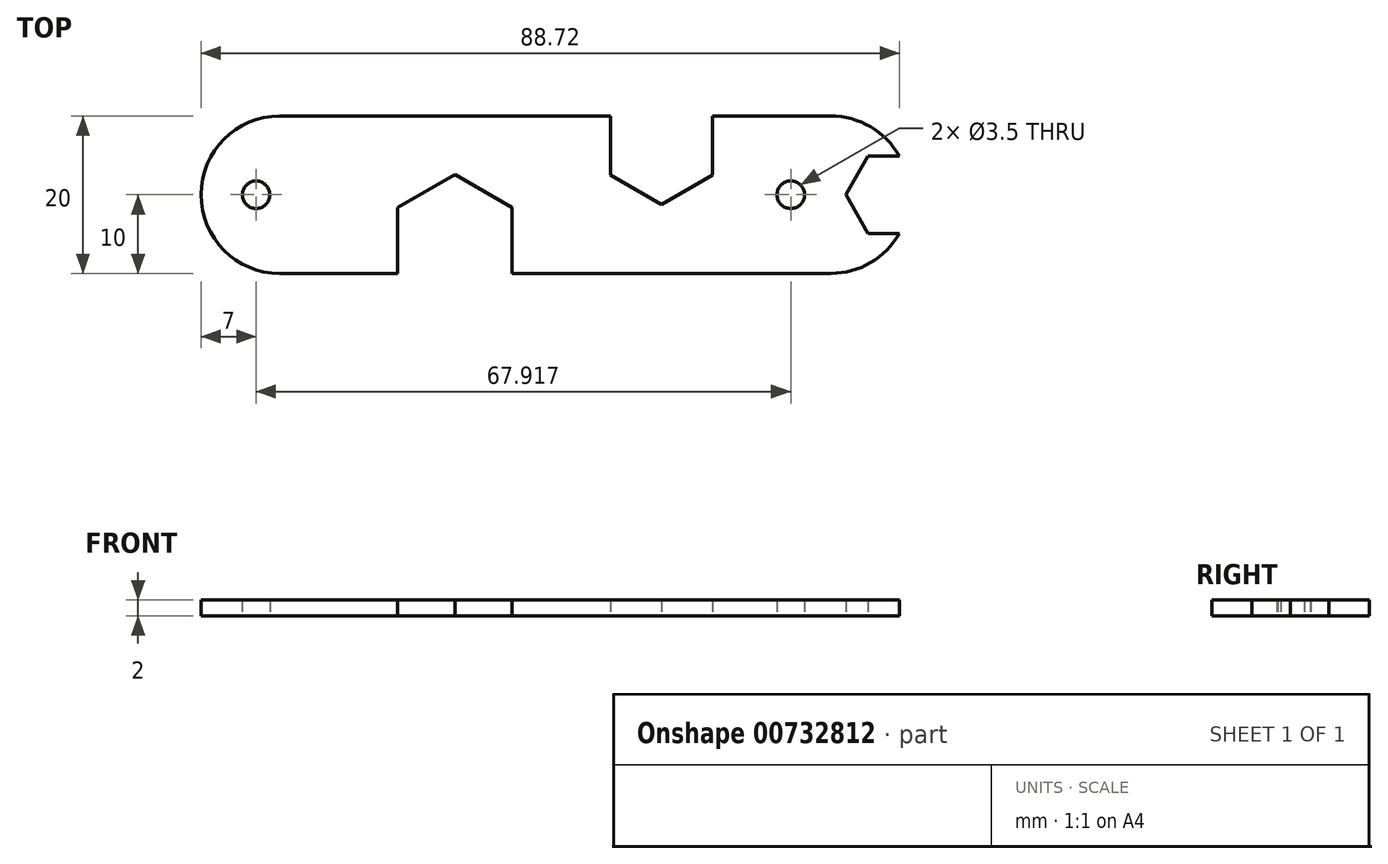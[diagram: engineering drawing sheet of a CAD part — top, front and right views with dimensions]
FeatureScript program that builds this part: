
annotation { "Feature Type Name" : "Feature", "Feature Type Description" : "" }
export const myFeature = defineFeature(function(context is Context, id is Id, definition is map)
    precondition{}
    {
        {
            var Q0;
            Q0=qCreatedBy(makeId("Top.planeOp"),FACE);
            var sketch = newSketch(context, id + "F0", { "sketchPlane" : qUnion([Q0])});
            skArc(sketch, "E0", {"start": v(36.44, 10) * mm, "mid": v(26.44, 0) * mm, "end": v(36.44, -10) * mm});
            skArc(sketch, "E1", {"start": v(106.44, -10) * mm, "mid": v(111.57, -8.59) * mm, "end": v(115.24, -4.74) * mm});
            skLineSegment(sketch, "E2", {"start": v(36.44, -10) * mm, "end": v(51.44, -10) * mm});
            skLineSegment(sketch, "E3", {"start": v(106.44, 10) * mm, "end": v(91.44, 10) * mm});
            skCircle(sketch, "E4.cCircle", {"center": v(58.69, -5.81) * mm, "radius": 7.25 * mm, "construction": true});
            skLineSegment(sketch, "E4.0", {"start": v(51.44, -10) * mm, "end": v(51.44, -1.63) * mm});
            skLineSegment(sketch, "E4.1", {"start": v(51.44, -1.63) * mm, "end": v(58.69, 2.56) * mm});
            skLineSegment(sketch, "E4.2", {"start": v(58.69, 2.56) * mm, "end": v(65.94, -1.63) * mm});
            skLineSegment(sketch, "E4.3", {"start": v(65.94, -1.63) * mm, "end": v(65.94, -10) * mm});
            skPoint(sketch, "E4.0.midPoint", {"position": v(51.44, -5.81) * mm});
            skCircle(sketch, "E5.cCircle", {"center": v(84.94, 6.25) * mm, "radius": 6.5 * mm, "construction": true});
            skLineSegment(sketch, "E5.0", {"start": v(78.44, 2.5) * mm, "end": v(78.44, 10) * mm});
            skLineSegment(sketch, "E5.3", {"start": v(91.44, 10) * mm, "end": v(91.44, 2.5) * mm});
            skLineSegment(sketch, "E5.4", {"start": v(91.44, 2.5) * mm, "end": v(84.94, -1.26) * mm});
            skLineSegment(sketch, "E5.5", {"start": v(84.94, -1.26) * mm, "end": v(78.44, 2.5) * mm});
            skPoint(sketch, "E5.0.midPoint", {"position": v(78.44, 6.25) * mm});
            skCircle(sketch, "E6.cCircle", {"center": v(114.01, 0) * mm, "radius": 4.9 * mm, "construction": true});
            skLineSegment(sketch, "E6.0", {"start": v(115.16, -4.9) * mm, "end": v(111.19, -4.9) * mm});
            skLineSegment(sketch, "E6.1", {"start": v(111.19, -4.9) * mm, "end": v(108.36, 0) * mm});
            skLineSegment(sketch, "E6.2", {"start": v(108.36, 0) * mm, "end": v(111.19, 4.9) * mm});
            skLineSegment(sketch, "E6.3", {"start": v(111.19, 4.9) * mm, "end": v(115.16, 4.9) * mm});
            skPoint(sketch, "E6.0.midPoint", {"position": v(114.01, -4.9) * mm});
            skCircle(sketch, "E7", {"center": v(33.44, 0) * mm, "radius": 1.75 * mm});
            skCircle(sketch, "E8", {"center": v(101.36, 0) * mm, "radius": 1.75 * mm});
            skArc(sketch, "E9.trimOffspring", {"start": v(115.24, 4.74) * mm, "mid": v(111.57, 8.59) * mm, "end": v(106.44, 10) * mm});
            skPoint(sketch, "E10.orphan", {"position": v(116.84, 4.9) * mm});
            skPoint(sketch, "E6.5.end.orphan", {"position": v(116.84, -4.9) * mm});
            skLineSegment(sketch, "E11.trimOffspring", {"start": v(78.44, 10) * mm, "end": v(36.44, 10) * mm});
            skPoint(sketch, "E12.orphan", {"position": v(84.94, 13.75) * mm});
            skLineSegment(sketch, "E13.trimOffspring", {"start": v(65.94, -10) * mm, "end": v(106.44, -10) * mm});
            skSolve(sketch);
        }
        {
            var Q0;
            Q0=qSketchRegion(id+"F0",true);
            extrude(context, id + "F1", {"entities" : qUnion([Q0]), "depth" : 2 * mm, "offsetDistance" : 25 * mm});
        }
    });
